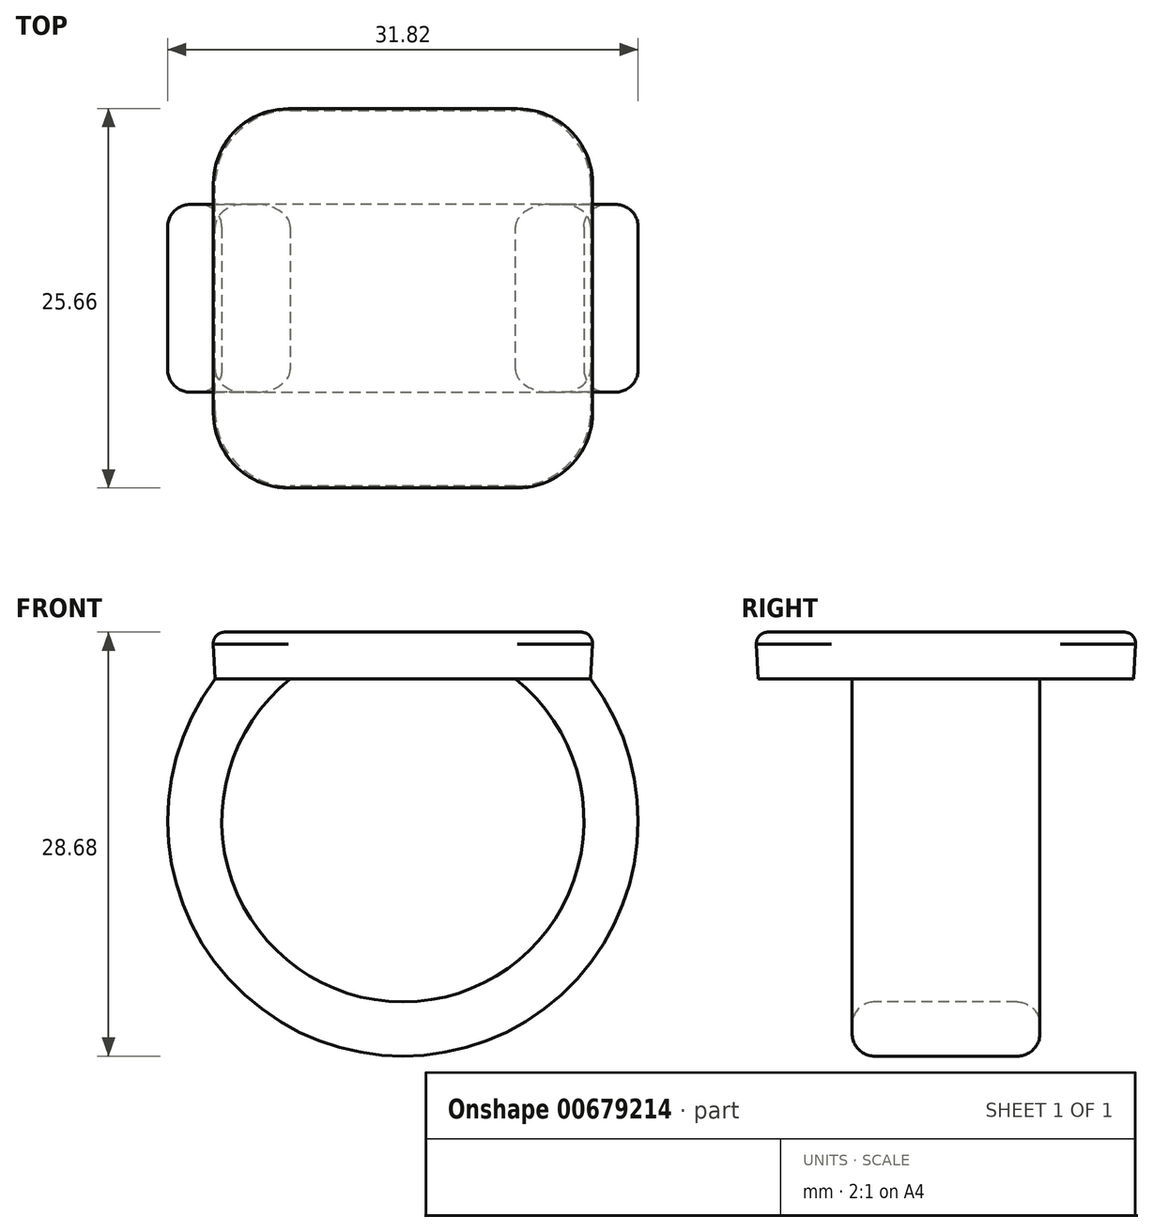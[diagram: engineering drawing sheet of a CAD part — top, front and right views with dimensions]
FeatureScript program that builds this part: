
annotation { "Feature Type Name" : "Feature", "Feature Type Description" : "" }
export const myFeature = defineFeature(function(context is Context, id is Id, definition is map)
    precondition{}
    {
        {
            var Q0;
            Q0=qCreatedBy(makeId("Top.planeOp"),FACE);
            var sketch = newSketch(context, id + "F0", { "sketchPlane" : qUnion([Q0])});
            skLineSegment(sketch, "E0.bottom", {"start": v(12.7, 12.7) * mm, "end": v(-12.7, 12.7) * mm});
            skLineSegment(sketch, "E0.top", {"start": v(12.7, -12.7) * mm, "end": v(-12.7, -12.7) * mm});
            skLineSegment(sketch, "E0.left", {"start": v(12.7, 12.7) * mm, "end": v(12.7, -12.7) * mm});
            skLineSegment(sketch, "E0.right", {"start": v(-12.7, 12.7) * mm, "end": v(-12.7, -12.7) * mm});
            skPoint(sketch, "E0.middle", {"position": v(0, 0) * mm});
            skSolve(sketch);
        }
        {
            var Q0;
            Q0 = qSketchRegion(id + "F0", true);
            extrude(context, id + "F1", {"entities" : qUnion([Q0]), "depth" : 3.17 * mm, "offsetDistance" : 25.4 * mm, "hasDraft" : true, "draftAngle" : 3 * degree});
        }
        {
            var Q0;
            Q0=qCreatedBy(makeId("Front.planeOp"),FACE);
            var sketch = newSketch(context, id + "F2", { "sketchPlane" : qUnion([Q0])});
            skArc(sketch, "E1", {"start": v(-10.16, 0) * mm, "mid": v(0, -23.56) * mm, "end": v(10.16, 0) * mm});
            skSolve(sketch);
        }
        {
            var Q0;
            Q0=makeQuery(id+"F1.opExtrude","CAP_FACE",FACE,{"disambiguationData":[OSD([sQuery(id+"F0.wireOp",EDGE,"E0.bottom"),sQuery(id+"F0.wireOp",EDGE,"E0.top"),sQuery(id+"F0.wireOp",EDGE,"E0.left"),sQuery(id+"F0.wireOp",EDGE,"E0.right")])],"isStart":true});
            var sketch = newSketch(context, id + "F3", { "sketchPlane" : qUnion([Q0])});
            skLineSegment(sketch, "E2.bottom", {"start": v(-7.62, -6.35) * mm, "end": v(-12.7, -6.35) * mm});
            skLineSegment(sketch, "E2.top", {"start": v(-7.62, 6.35) * mm, "end": v(-12.7, 6.35) * mm});
            skLineSegment(sketch, "E2.left", {"start": v(-7.62, -6.35) * mm, "end": v(-7.62, 6.35) * mm});
            skLineSegment(sketch, "E2.right", {"start": v(-12.7, -6.35) * mm, "end": v(-12.7, 6.35) * mm});
            skPoint(sketch, "E2.middle", {"position": v(-10.16, 0) * mm});
            skSolve(sketch);
        }
        {
            var Q0;
            Q0 = qSketchRegion(id + "F3", true);
            var Q1;
            Q1 = qConstructionFilter(qBodyType(qCreatedBy(id + "F2" ,EDGE), BodyType.WIRE), ConstructionObject.NO);
            sweep(context, id + "F4", {"operationType" : NewBodyOperationType.ADD, "profiles" : qUnion([Q0]), "path" : qUnion([Q1])});
        }
        {
            var Q0;
            Q0=qCreatedBy(makeId("Front.planeOp"),FACE);
            var sketch = newSketch(context, id + "F5", { "sketchPlane" : qUnion([Q0])});
            skLineSegment(sketch, "E3.0", {"start": v(10.16, 0) * mm, "end": v(7.62, 0) * mm});
            skLineSegment(sketch, "E3.1", {"start": v(10.01, -2.54) * mm, "end": v(10.16, 0) * mm});
            skArc(sketch, "E3.2", {"start": v(10.01, -2.54) * mm, "mid": v(8.9, -1.18) * mm, "end": v(7.62, 0) * mm});
            skLineSegment(sketch, "E4.trimOffspring", {"start": v(-7.62, 0) * mm, "end": v(-12.7, 0) * mm});
            skPoint(sketch, "E5.orphan", {"position": v(12.7, 0) * mm});
            skSolve(sketch);
        }
        {
            var Q0;
            Q0=makeQuery(id+"F5.imprint","IMPRINT",FACE,{"disambiguationData":[TD([[makeQuery(id+"F5.imprint","IMPRINT",EDGE,{"derivedFrom":sQuery(id+"F5.wireOp",EDGE,"E3.0")}),1.0]])]});
            var Q1;
            Q1=makeQuery(id+"F4.opSweep","SWEPT_FACE",FACE,{"disambiguationData":[OSD([sQuery(id+"F2.wireOp",EDGE,"E1"),sQuery(id+"F3.wireOp",EDGE,"E2.top")])]});
            var Q2;
            Q2=makeQuery(id+"F4.opSweep","SWEPT_FACE",FACE,{"disambiguationData":[OSD([sQuery(id+"F2.wireOp",EDGE,"E1"),sQuery(id+"F3.wireOp",EDGE,"E2.bottom")])]});
            extrude(context, id + "F6", {"entities" : qUnion([Q0]), "operationType" : NewBodyOperationType.ADD, "endBound" : BoundingType.UP_TO_SURFACE, "depth" : 25.4 * mm, "endBoundEntityFace" : qUnion([Q1]), "offsetDistance" : 25.4 * mm, "hasSecondDirection" : true, "secondDirectionBound" : SecondDirectionBoundingType.UP_TO_SURFACE, "secondDirectionOppositeDirection" : true, "secondDirectionDepth" : 25.4 * mm, "secondDirectionBoundEntityFace" : qUnion([Q2])});
        }
        {
            var Q0;
            Q0=makeQuery(id+"F1.opExtrude","SWEPT_EDGE",EDGE,{"disambiguationData":[OSD([sQuery(id+"F0.wireOp",EDGE,"E0.top"),sQuery(id+"F0.wireOp",EDGE,"E0.left")])]});
            var Q1;
            Q1=makeQuery(id+"F1.opExtrude","SWEPT_EDGE",EDGE,{"disambiguationData":[OSD([sQuery(id+"F0.wireOp",EDGE,"E0.bottom"),sQuery(id+"F0.wireOp",EDGE,"E0.left")])]});
            var Q2;
            Q2=makeQuery(id+"F1.opExtrude","SWEPT_EDGE",EDGE,{"disambiguationData":[OSD([sQuery(id+"F0.wireOp",EDGE,"E0.bottom"),sQuery(id+"F0.wireOp",EDGE,"E0.right")])]});
            var Q3;
            Q3=makeQuery(id+"F1.opExtrude","SWEPT_EDGE",EDGE,{"disambiguationData":[OSD([sQuery(id+"F0.wireOp",EDGE,"E0.top"),sQuery(id+"F0.wireOp",EDGE,"E0.right")])]});
            fillet(context, id + "F7", {"entities" : qUnion([Q0, Q1, Q2, Q3]), "radius" : 5.08 * mm, "tangentPropagation" : true, "allowEdgeOverflow" : false});
        }
        {
            var Q0;
            {var subQ0=sQuery(id+"F3.wireOp",EDGE,"E2.top");var subQ1=sQuery(id+"F2.wireOp",EDGE,"E1");Q0=makeQuery(id+"F6.boolean.opBoolean","MERGE",EDGE,{"derivedFrom":[makeQuery(id+"F4.opSweep","SWEPT_EDGE",EDGE,{"disambiguationData":[OSD([subQ1,subQ0,sQuery(id+"F3.wireOp",EDGE,"E2.left")])]}),makeQuery(id+"F6.opExtrude","TWEAK_EDGE",EDGE,{"derivedFrom":[makeQuery(id+"F4.opSweep","SWEPT_FACE",FACE,{"disambiguationData":[OSD([subQ1,subQ0])]}),makeQuery(id+"F5.imprint","IMPRINT",EDGE,{"derivedFrom":sQuery(id+"F5.wireOp",EDGE,"E3.2")})]})]});}
            var Q1;
            Q1=makeQuery(id+"F4.opSweep","SWEPT_EDGE",EDGE,{"disambiguationData":[OSD([sQuery(id+"F0.wireOp",EDGE,"E0.right"),sQuery(id+"F2.wireOp",EDGE,"E1"),sQuery(id+"F3.wireOp",EDGE,"E2.top"),sQuery(id+"F3.wireOp",EDGE,"E2.right")])]});
            var Q2;
            Q2=makeQuery(id+"F4.opSweep","SWEPT_EDGE",EDGE,{"disambiguationData":[OSD([sQuery(id+"F0.wireOp",EDGE,"E0.right"),sQuery(id+"F2.wireOp",EDGE,"E1"),sQuery(id+"F3.wireOp",EDGE,"E2.bottom"),sQuery(id+"F3.wireOp",EDGE,"E2.right")])]});
            var Q3;
            {var subQ0=sQuery(id+"F3.wireOp",EDGE,"E2.bottom");var subQ1=sQuery(id+"F2.wireOp",EDGE,"E1");Q3=makeQuery(id+"F6.boolean.opBoolean","MERGE",EDGE,{"derivedFrom":[makeQuery(id+"F4.opSweep","SWEPT_EDGE",EDGE,{"disambiguationData":[OSD([subQ1,subQ0,sQuery(id+"F3.wireOp",EDGE,"E2.left")])]}),makeQuery(id+"F6.opExtrude","TWEAK_EDGE",EDGE,{"derivedFrom":[makeQuery(id+"F4.opSweep","SWEPT_FACE",FACE,{"disambiguationData":[OSD([subQ1,subQ0])]}),makeQuery(id+"F5.imprint","IMPRINT",EDGE,{"derivedFrom":sQuery(id+"F5.wireOp",EDGE,"E3.2")})]})]});}
            fillet(context, id + "F8", {"entities" : qUnion([Q0, Q1, Q2, Q3]), "radius" : 1.52 * mm, "tangentPropagation" : true, "allowEdgeOverflow" : false});
        }
        {
            var Q0;
            Q0=makeQuery(id+"F1.opExtrude","CAP_EDGE",EDGE,{"disambiguationData":[OSD([sQuery(id+"F0.wireOp",EDGE,"E0.top")])],"isStart":false});
            var Q1;
            {var subQ0=sQuery(id+"F0.wireOp",EDGE,"E0.right");var subQ1=sQuery(id+"F0.wireOp",EDGE,"E0.top");Q1=makeQuery(id+"F7.opFillet","BLEND_EDGE",EDGE,{"blendedFrom":[makeQuery(id+"F1.opExtrude","SWEPT_EDGE",EDGE,{"disambiguationData":[OSD([subQ1,subQ0])]}),makeQuery(id+"F1.opExtrude","CAP_FACE",FACE,{"disambiguationData":[OSD([sQuery(id+"F0.wireOp",EDGE,"E0.bottom"),subQ1,sQuery(id+"F0.wireOp",EDGE,"E0.left"),subQ0])],"isStart":false})],"blendedInto":[makeQuery(id+"F1.opExtrude","CAP_FACE",FACE,{"disambiguationData":[OSD([sQuery(id+"F0.wireOp",EDGE,"E0.bottom"),subQ1,sQuery(id+"F0.wireOp",EDGE,"E0.left"),subQ0])],"isStart":false})]});}
            var Q2;
            Q2=makeQuery(id+"F1.opExtrude","CAP_FACE",FACE,{"disambiguationData":[OSD([sQuery(id+"F0.wireOp",EDGE,"E0.bottom"),sQuery(id+"F0.wireOp",EDGE,"E0.top"),sQuery(id+"F0.wireOp",EDGE,"E0.left"),sQuery(id+"F0.wireOp",EDGE,"E0.right")])],"isStart":false});
            fillet(context, id + "F9", {"entities" : qUnion([Q0, Q1, Q2]), "radius" : 0.76 * mm, "tangentPropagation" : true, "allowEdgeOverflow" : false});
        }
    });
